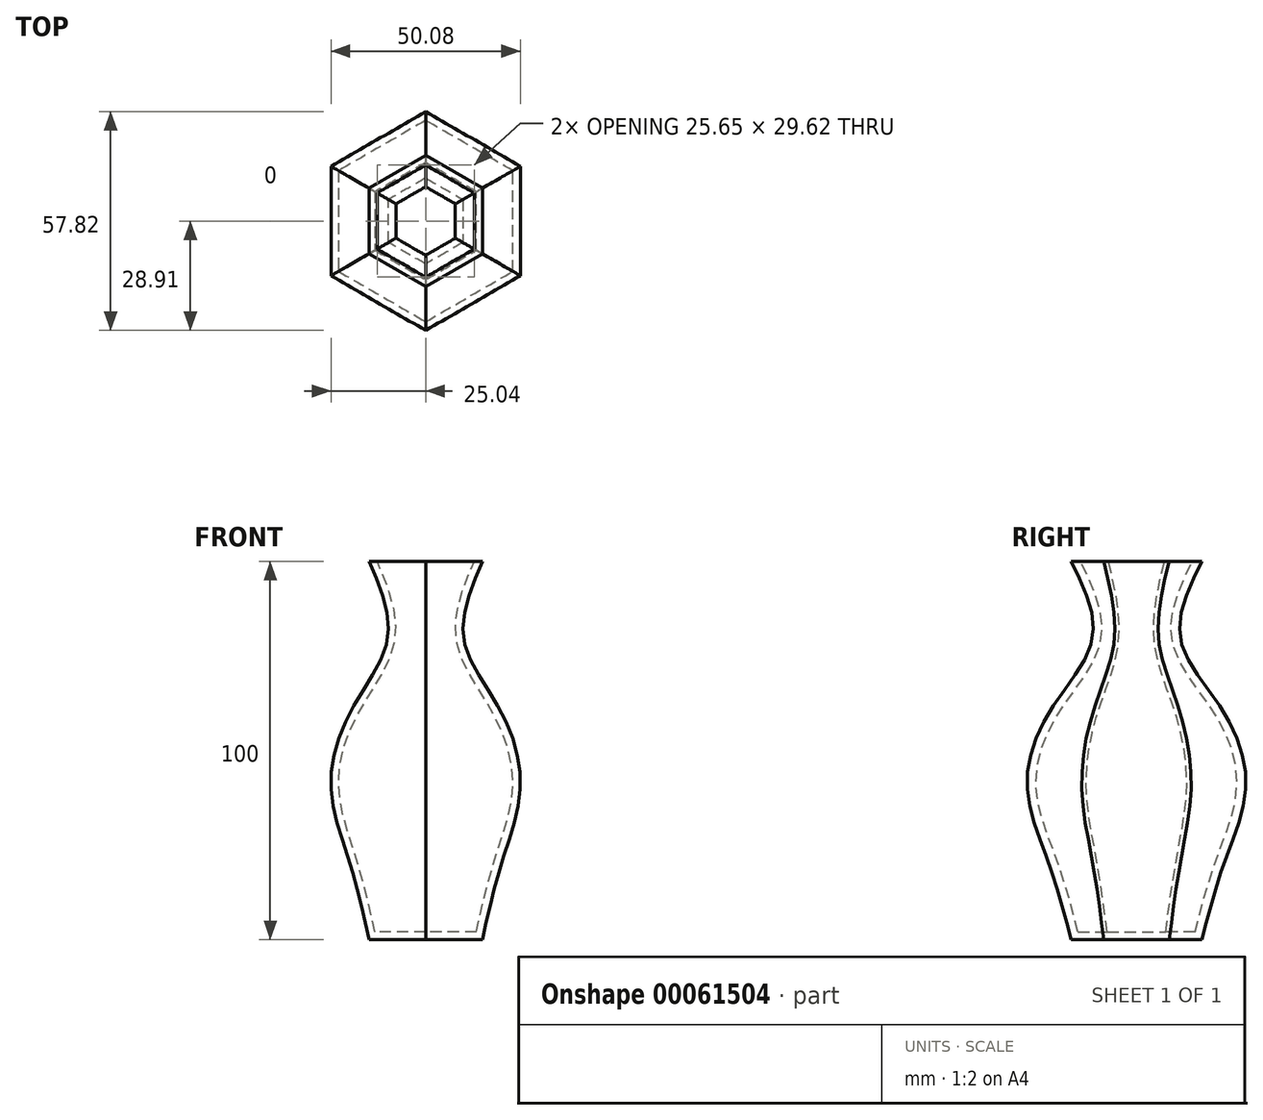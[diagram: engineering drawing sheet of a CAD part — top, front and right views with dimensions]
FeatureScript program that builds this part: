
annotation { "Feature Type Name" : "Feature", "Feature Type Description" : "" }
export const myFeature = defineFeature(function(context is Context, id is Id, definition is map)
    precondition{}
    {
        {
            var Q0;
            Q0=qCreatedBy(makeId("Top.planeOp"),FACE);
            var sketch = newSketch(context, id + "F0", { "sketchPlane" : qUnion([Q0])});
            skCircle(sketch, "E0.cCircle", {"center": v(0, 0) * mm, "radius": 25 * mm, "construction": true});
            skLineSegment(sketch, "E0.0", {"start": v(25, 14.43) * mm, "end": v(25, -14.43) * mm});
            skLineSegment(sketch, "E0.1", {"start": v(25, -14.43) * mm, "end": v(0, -28.87) * mm});
            skLineSegment(sketch, "E0.2", {"start": v(0, -28.87) * mm, "end": v(-25, -14.43) * mm});
            skLineSegment(sketch, "E0.3", {"start": v(-25, -14.43) * mm, "end": v(-25, 14.43) * mm});
            skLineSegment(sketch, "E0.4", {"start": v(-25, 14.43) * mm, "end": v(0, 28.87) * mm});
            skLineSegment(sketch, "E0.5", {"start": v(0, 28.87) * mm, "end": v(25, 14.43) * mm});
            skPoint(sketch, "E0.0.midPoint", {"position": v(25, 0) * mm});
            skCircle(sketch, "E1.cCircle", {"center": v(0, 0) * mm, "radius": 20 * mm, "construction": true});
            skLineSegment(sketch, "E1.0", {"start": v(20, 11.55) * mm, "end": v(20, -11.55) * mm});
            skLineSegment(sketch, "E1.1", {"start": v(20, -11.55) * mm, "end": v(0, -23.1) * mm});
            skLineSegment(sketch, "E1.2", {"start": v(0, -23.1) * mm, "end": v(-20, -11.55) * mm});
            skLineSegment(sketch, "E1.3", {"start": v(-20, -11.55) * mm, "end": v(-20, 11.55) * mm});
            skLineSegment(sketch, "E1.4", {"start": v(-20, 11.55) * mm, "end": v(0, 23.1) * mm});
            skLineSegment(sketch, "E1.5", {"start": v(0, 23.1) * mm, "end": v(20, 11.55) * mm});
            skPoint(sketch, "E1.0.midPoint", {"position": v(20, 0) * mm});
            skCircle(sketch, "E2.cCircle", {"center": v(0, 0) * mm, "radius": 15 * mm, "construction": true});
            skLineSegment(sketch, "E2.0", {"start": v(15, 8.66) * mm, "end": v(15, -8.66) * mm});
            skLineSegment(sketch, "E2.1", {"start": v(15, -8.66) * mm, "end": v(0, -17.32) * mm});
            skLineSegment(sketch, "E2.2", {"start": v(0, -17.32) * mm, "end": v(-15, -8.66) * mm});
            skLineSegment(sketch, "E2.3", {"start": v(-15, -8.66) * mm, "end": v(-15, 8.66) * mm});
            skLineSegment(sketch, "E2.4", {"start": v(-15, 8.66) * mm, "end": v(0, 17.32) * mm});
            skLineSegment(sketch, "E2.5", {"start": v(0, 17.32) * mm, "end": v(15, 8.66) * mm});
            skPoint(sketch, "E2.0.midPoint", {"position": v(15, 0) * mm});
            skCircle(sketch, "E3.cCircle", {"center": v(0, 0) * mm, "radius": 10 * mm, "construction": true});
            skLineSegment(sketch, "E3.0", {"start": v(10, 5.77) * mm, "end": v(10, -5.77) * mm});
            skLineSegment(sketch, "E3.1", {"start": v(10, -5.77) * mm, "end": v(0, -11.55) * mm});
            skLineSegment(sketch, "E3.2", {"start": v(0, -11.55) * mm, "end": v(-10, -5.77) * mm});
            skLineSegment(sketch, "E3.3", {"start": v(-10, -5.77) * mm, "end": v(-10, 5.77) * mm});
            skLineSegment(sketch, "E3.4", {"start": v(-10, 5.77) * mm, "end": v(0, 11.55) * mm});
            skLineSegment(sketch, "E3.5", {"start": v(0, 11.55) * mm, "end": v(10, 5.77) * mm});
            skPoint(sketch, "E3.0.midPoint", {"position": v(10, 0) * mm});
            skSolve(sketch);
        }
        {
            var Q0;
            Q0=qCreatedBy(makeId("Top.planeOp"),FACE);
            var sketch = newSketch(context, id + "F1", { "sketchPlane" : qUnion([Q0])});
            skLineSegment(sketch, "E4.0", {"start": v(-15, 8.66) * mm, "end": v(0, 17.32) * mm});
            skLineSegment(sketch, "E5.0", {"start": v(0, 17.32) * mm, "end": v(15, 8.66) * mm});
            skLineSegment(sketch, "E6.0", {"start": v(15, 8.66) * mm, "end": v(15, -8.66) * mm});
            skLineSegment(sketch, "E7.0", {"start": v(15, -8.66) * mm, "end": v(0, -17.32) * mm});
            skLineSegment(sketch, "E8.0", {"start": v(0, -17.32) * mm, "end": v(-15, -8.66) * mm});
            skLineSegment(sketch, "E9.0", {"start": v(-15, -8.66) * mm, "end": v(-15, 8.66) * mm});
            skSolve(sketch);
        }
        {
            var Q0;
            Q0=qCreatedBy(makeId("Top.planeOp"),FACE);
            cPlane(context, id + "F2", {"entities" : qUnion([Q0]), "cplaneType" : CPlaneType.OFFSET, "offset" : 20 * mm, "width" : 150 * mm, "height" : 150 * mm});
        }
        {
            var Q0;
            Q0=qCreatedBy(id+"F2.planeOp",FACE);
            cPlane(context, id + "F3", {"entities" : qUnion([Q0]), "cplaneType" : CPlaneType.OFFSET, "offset" : 20 * mm, "width" : 150 * mm, "height" : 150 * mm});
        }
        {
            var Q0;
            Q0=qCreatedBy(id+"F3.planeOp",FACE);
            cPlane(context, id + "F4", {"entities" : qUnion([Q0]), "cplaneType" : CPlaneType.OFFSET, "offset" : 20 * mm, "width" : 150 * mm, "height" : 150 * mm});
        }
        {
            var Q0;
            Q0=qCreatedBy(id+"F4.planeOp",FACE);
            cPlane(context, id + "F5", {"entities" : qUnion([Q0]), "cplaneType" : CPlaneType.OFFSET, "offset" : 20 * mm, "width" : 150 * mm, "height" : 150 * mm});
        }
        {
            var Q0;
            Q0=qCreatedBy(id+"F5.planeOp",FACE);
            cPlane(context, id + "F6", {"entities" : qUnion([Q0]), "cplaneType" : CPlaneType.OFFSET, "offset" : 20 * mm, "width" : 150 * mm, "height" : 150 * mm});
        }
        {
            var Q0;
            Q0=qCreatedBy(id+"F2.planeOp",FACE);
            var sketch = newSketch(context, id + "F7", { "sketchPlane" : qUnion([Q0])});
            skLineSegment(sketch, "E10.0", {"start": v(0, 23.1) * mm, "end": v(20, 11.55) * mm});
            skLineSegment(sketch, "E11.0", {"start": v(20, 11.55) * mm, "end": v(20, -11.55) * mm});
            skLineSegment(sketch, "E12.0", {"start": v(20, -11.55) * mm, "end": v(0, -23.1) * mm});
            skLineSegment(sketch, "E13.0", {"start": v(0, -23.1) * mm, "end": v(-20, -11.55) * mm});
            skLineSegment(sketch, "E14.0", {"start": v(-20, -11.55) * mm, "end": v(-20, 11.55) * mm});
            skLineSegment(sketch, "E15.0", {"start": v(-20, 11.55) * mm, "end": v(0, 23.1) * mm});
            skSolve(sketch);
        }
        {
            var Q0;
            Q0=qCreatedBy(id+"F3.planeOp",FACE);
            var sketch = newSketch(context, id + "F8", { "sketchPlane" : qUnion([Q0])});
            skLineSegment(sketch, "E16.0", {"start": v(-25, 14.43) * mm, "end": v(0, 28.87) * mm});
            skLineSegment(sketch, "E17.0", {"start": v(0, 28.87) * mm, "end": v(25, 14.43) * mm});
            skLineSegment(sketch, "E18.0", {"start": v(25, 14.43) * mm, "end": v(25, -14.43) * mm});
            skLineSegment(sketch, "E19.0", {"start": v(25, -14.43) * mm, "end": v(0, -28.87) * mm});
            skLineSegment(sketch, "E20.0", {"start": v(0, -28.87) * mm, "end": v(-25, -14.43) * mm});
            skLineSegment(sketch, "E21.0", {"start": v(-25, -14.43) * mm, "end": v(-25, 14.43) * mm});
            skSolve(sketch);
        }
        {
            var Q0;
            Q0=qCreatedBy(id+"F4.planeOp",FACE);
            var sketch = newSketch(context, id + "F9", { "sketchPlane" : qUnion([Q0])});
            skLineSegment(sketch, "E22.0", {"start": v(0, 23.1) * mm, "end": v(20, 11.55) * mm});
            skLineSegment(sketch, "E23.0", {"start": v(-20, 11.55) * mm, "end": v(0, 23.1) * mm});
            skLineSegment(sketch, "E24.0", {"start": v(-20, -11.55) * mm, "end": v(-20, 11.55) * mm});
            skLineSegment(sketch, "E25.0", {"start": v(0, -23.1) * mm, "end": v(-20, -11.55) * mm});
            skLineSegment(sketch, "E26.0", {"start": v(20, -11.55) * mm, "end": v(0, -23.1) * mm});
            skLineSegment(sketch, "E27.0", {"start": v(20, 11.55) * mm, "end": v(20, -11.55) * mm});
            skSolve(sketch);
        }
        {
            var Q0;
            Q0=qCreatedBy(id+"F5.planeOp",FACE);
            var sketch = newSketch(context, id + "F10", { "sketchPlane" : qUnion([Q0])});
            skLineSegment(sketch, "E28.0", {"start": v(-10, 5.77) * mm, "end": v(0, 11.55) * mm});
            skLineSegment(sketch, "E29.0", {"start": v(0, 11.55) * mm, "end": v(10, 5.77) * mm});
            skLineSegment(sketch, "E30.0", {"start": v(10, 5.77) * mm, "end": v(10, -5.77) * mm});
            skLineSegment(sketch, "E31.0", {"start": v(10, -5.77) * mm, "end": v(0, -11.55) * mm});
            skLineSegment(sketch, "E32.0", {"start": v(0, -11.55) * mm, "end": v(-10, -5.77) * mm});
            skLineSegment(sketch, "E33.0", {"start": v(-10, -5.77) * mm, "end": v(-10, 5.77) * mm});
            skSolve(sketch);
        }
        {
            var Q0;
            Q0=qCreatedBy(id+"F6.planeOp",FACE);
            var sketch = newSketch(context, id + "F11", { "sketchPlane" : qUnion([Q0])});
            skLineSegment(sketch, "E34.0", {"start": v(-15, 8.66) * mm, "end": v(0, 17.32) * mm});
            skLineSegment(sketch, "E35.0", {"start": v(0, 17.32) * mm, "end": v(15, 8.66) * mm});
            skLineSegment(sketch, "E36.0", {"start": v(15, 8.66) * mm, "end": v(15, -8.66) * mm});
            skLineSegment(sketch, "E37.0", {"start": v(15, -8.66) * mm, "end": v(0, -17.32) * mm});
            skLineSegment(sketch, "E38.0", {"start": v(0, -17.32) * mm, "end": v(-15, -8.66) * mm});
            skLineSegment(sketch, "E39.0", {"start": v(-15, -8.66) * mm, "end": v(-15, 8.66) * mm});
            skSolve(sketch);
        }
        {
            var Q0;
            Q0=makeQuery(id+"F1.imprint","IMPRINT",FACE,{"disambiguationData":[TD([[makeQuery(id+"F1.imprint","IMPRINT",EDGE,{"derivedFrom":sQuery(id+"F1.wireOp",EDGE,"E4.0")}),-1.0]])]});
            var Q1;
            Q1=makeQuery(id+"F7.imprint","IMPRINT",FACE,{"disambiguationData":[TD([[makeQuery(id+"F7.imprint","IMPRINT",EDGE,{"derivedFrom":sQuery(id+"F7.wireOp",EDGE,"E10.0")}),-1.0]])]});
            var Q2;
            Q2=makeQuery(id+"F8.imprint","IMPRINT",FACE,{"disambiguationData":[TD([[makeQuery(id+"F8.imprint","IMPRINT",EDGE,{"derivedFrom":sQuery(id+"F8.wireOp",EDGE,"E16.0")}),-1.0]])]});
            var Q3;
            Q3=makeQuery(id+"F9.imprint","IMPRINT",FACE,{"disambiguationData":[TD([[makeQuery(id+"F9.imprint","IMPRINT",EDGE,{"derivedFrom":sQuery(id+"F9.wireOp",EDGE,"E22.0")}),-1.0]])]});
            var Q4;
            Q4=makeQuery(id+"F10.imprint","IMPRINT",FACE,{"disambiguationData":[TD([[makeQuery(id+"F10.imprint","IMPRINT",EDGE,{"derivedFrom":sQuery(id+"F10.wireOp",EDGE,"E28.0")}),-1.0]])]});
            var Q5;
            Q5=makeQuery(id+"F11.imprint","IMPRINT",FACE,{"disambiguationData":[TD([[makeQuery(id+"F11.imprint","IMPRINT",EDGE,{"derivedFrom":sQuery(id+"F11.wireOp",EDGE,"E34.0")}),-1.0]])]});
            loft(context, id + "F12", {"sheetProfilesArray" : [{ "sheetProfileEntities" : qUnion([Q0]) }, { "sheetProfileEntities" : qUnion([Q1]) }, { "sheetProfileEntities" : qUnion([Q2]) }, { "sheetProfileEntities" : qUnion([Q3]) }, { "sheetProfileEntities" : qUnion([Q4]) }, { "sheetProfileEntities" : qUnion([Q5]) }]});
        }
        {
            var Q0;
            Q0=makeQuery(id+"F12.opLoft","CAP_FACE",FACE,{"disambiguationData":[OSD([makeQuery(id+"F11.imprint","IMPRINT",FACE,{"disambiguationData":[TD([[makeQuery(id+"F11.imprint","IMPRINT",EDGE,{"derivedFrom":sQuery(id+"F11.wireOp",EDGE,"E34.0")}),-1.0]])]})])],"isStart":true});
            shell(context, id + "F13", {"entities" : qUnion([Q0]), "thickness" : 2 * mm});
        }
    });
